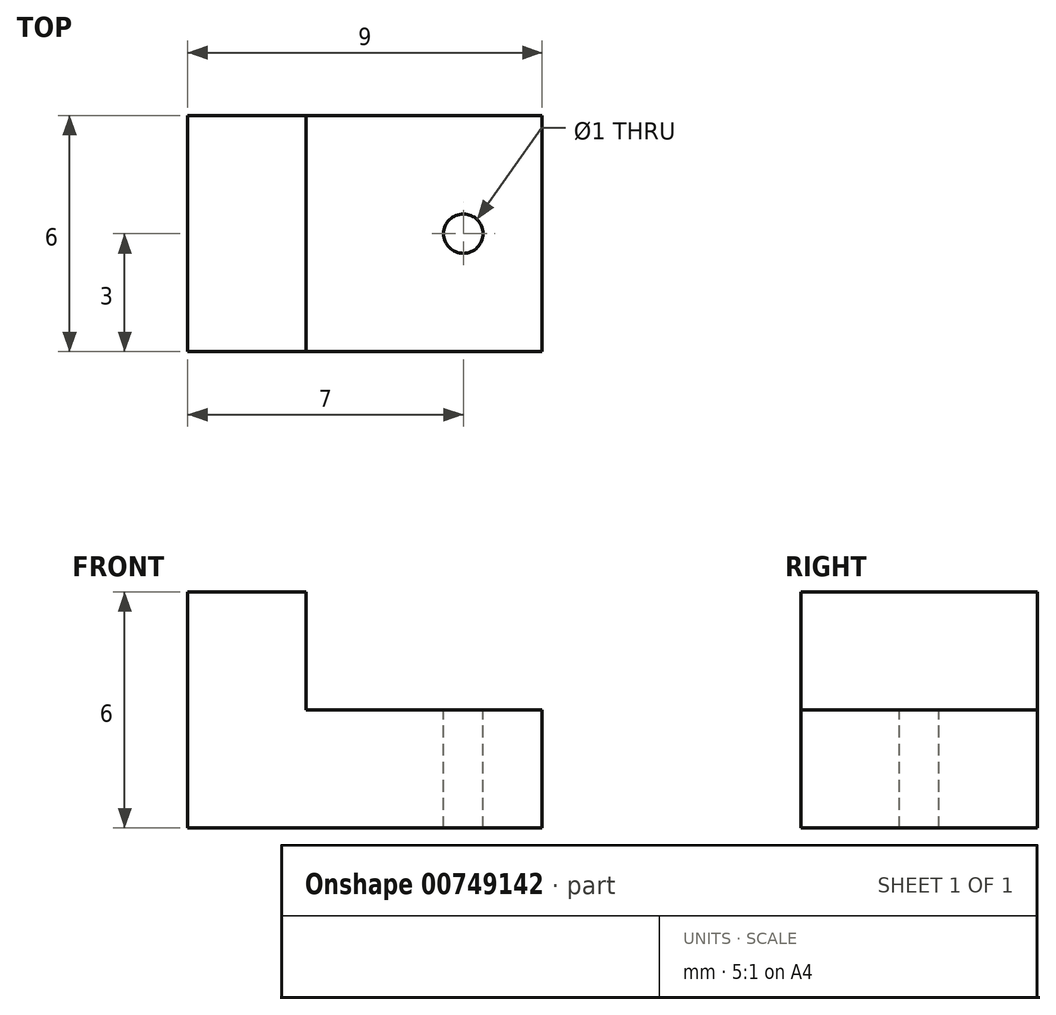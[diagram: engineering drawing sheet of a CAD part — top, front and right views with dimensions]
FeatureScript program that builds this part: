
annotation { "Feature Type Name" : "Feature", "Feature Type Description" : "" }
export const myFeature = defineFeature(function(context is Context, id is Id, definition is map)
    precondition{}
    {
        {
            var Q0;
            Q0=qCreatedBy(makeId("Front.planeOp"),FACE);
            var sketch = newSketch(context, id + "F0", { "sketchPlane" : qUnion([Q0])});
            skLineSegment(sketch, "E0", {"start": v(0, 0) * mm, "end": v(9, 0) * mm});
            skLineSegment(sketch, "E1", {"start": v(9, 0) * mm, "end": v(9, 3) * mm});
            skLineSegment(sketch, "E2", {"start": v(9, 3) * mm, "end": v(3, 3) * mm});
            skLineSegment(sketch, "E3", {"start": v(3, 3) * mm, "end": v(3, 6) * mm});
            skLineSegment(sketch, "E4", {"start": v(3, 6) * mm, "end": v(0, 6) * mm});
            skLineSegment(sketch, "E5", {"start": v(0, 6) * mm, "end": v(0, 0) * mm});
            skSolve(sketch);
        }
        {
            var Q0;
            Q0 = qSketchRegion(id + "F0", true);
            extrude(context, id + "F1", {"entities" : qUnion([Q0]), "depth" : 6 * mm, "offsetDistance" : 25 * mm});
        }
        {
            var Q0;
            Q0=makeQuery(id+"F1.opExtrude","SWEPT_FACE",FACE,{"disambiguationData":[OSD([sQuery(id+"F0.wireOp",EDGE,"E2")])]});
            var sketch = newSketch(context, id + "F2", { "sketchPlane" : qUnion([Q0])});
            skLineSegment(sketch, "E6", {"start": v(3, -6) * mm, "end": v(9, -6) * mm, "construction": true});
            skLineSegment(sketch, "E7", {"start": v(9, -6) * mm, "end": v(9, 0) * mm, "construction": true});
            skLineSegment(sketch, "E8", {"start": v(9, 0) * mm, "end": v(3, 0) * mm, "construction": true});
            skLineSegment(sketch, "E9", {"start": v(3, 0) * mm, "end": v(3, -6) * mm, "construction": true});
            skPoint(sketch, "E10.centerSnap0", {"position": v(6, -6) * mm});
            skCircle(sketch, "E11", {"center": v(7, -3) * mm, "radius": 0.5 * mm});
            skLineSegment(sketch, "E12", {"start": v(7, -3) * mm, "end": v(9, -3) * mm, "construction": true});
            skSolve(sketch);
        }
        {
            var Q0;
            Q0=makeQuery(id+"F2.imprint","IMPRINT",FACE,{"disambiguationData":[TD([[makeQuery(id+"F2.imprint","IMPRINT",EDGE,{"derivedFrom":sQuery(id+"F2.wireOp",EDGE,"E11")}),1.0]])]});
            extrude(context, id + "F3", {"entities" : qUnion([Q0]), "operationType" : NewBodyOperationType.REMOVE, "oppositeDirection" : true, "depth" : 6 * mm, "offsetDistance" : 25 * mm});
        }
    });
